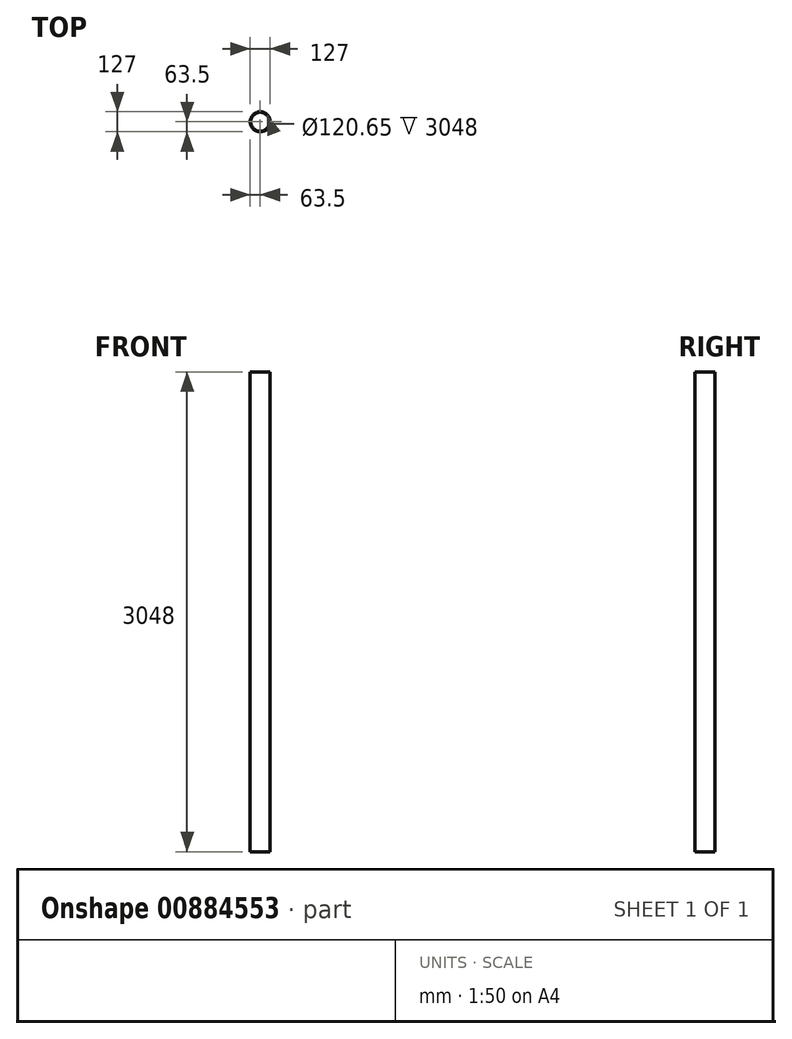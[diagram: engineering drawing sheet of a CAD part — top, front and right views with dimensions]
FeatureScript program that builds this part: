
annotation { "Feature Type Name" : "Feature", "Feature Type Description" : "" }
export const myFeature = defineFeature(function(context is Context, id is Id, definition is map)
    precondition{}
    {
        {
            var Q0;
            Q0=qCreatedBy(makeId("Top.planeOp"),FACE);
            var sketch = newSketch(context, id + "F0", { "sketchPlane" : qUnion([Q0])});
            skCircle(sketch, "E0", {"center": v(0, 0) * mm, "radius": 63.5 * mm});
            skCircle(sketch, "E1", {"center": v(0, 0) * mm, "radius": 60.33 * mm});
            skSolve(sketch);
        }
        {
            var Q0;
            Q0=makeQuery(id+"F0.imprint","IMPRINT",FACE,{"disambiguationData":[TD([[makeQuery(id+"F0.imprint","IMPRINT",EDGE,{"derivedFrom":sQuery(id+"F0.wireOp",EDGE,"E0")}),1.0]])]});
            extrude(context, id + "F1", {"entities" : qUnion([Q0]), "depth" : 3048 * mm, "offsetDistance" : 25.4 * mm});
        }
    });
